# Revit family: Planter-Raised_Bed-CityScapes-Planx
name_source: partatom
category: Specialty Equipment
units: mm (PartAtom-declared; Revit-internal decimal feet)

## family parameters
Always vertical = Yes
Cut with Voids When Loaded = No
Enable Cutting in Views = No
Maintain Annotation Orientation = No
Part Type = Normal
Room Calculation Point = No
Round Connector Dimension = Use Diameter
Shared = No
Work Plane-Based = No

## types (12) — shared parameters
CAD Details = https://www.arcat.com
Default Elevation = 0"
Description = Raised Bed Planter
Keynote = 32 94 33
Manufacturer = CityScapes
Model = Planx Planters - Raised Bed Series
Product Page URL = https://www.arcat.com
Specification = https://www.arcat.com
URL = https://cityscapesinc.com

## per-type parameters (varying)
| type | 2 Planks | 3 Planks | Height | Length | Width |
| 24”x24”x12” | Yes | No | 12" | 24" | 48" |
| 24”x48”x12” | Yes | No | 12" | 24" | 48" |
| 48”x48”x18” | No | Yes | 18" | 48" | 48" |
| 24”x96”x12” | Yes | No | 12" | 24" | 96" |
| 24”x24”x18” | No | Yes | 18" | 24" | 24" |
| 24”x48”x18” | No | Yes | 18" | 24" | 48" |
| 24”x96”x18” | No | Yes | 18" | 24" | 96" |
| 48”x48”x12” | Yes | No | 12" | 48" | 48" |
| 48”x96”x12” | Yes | No | 12" | 48" | 96" |
| 48”x96”x18” | No | Yes | 18" | 48" | 96" |
| 48”x120”x18” | No | Yes | 18" | 48" | 120" |
| 48”x120”x12” | Yes | No | 12" | 48" | 120" |

## geometry (parser evidence)
native form markers: Sweep x3
no freeform markers — native parametric forms only
